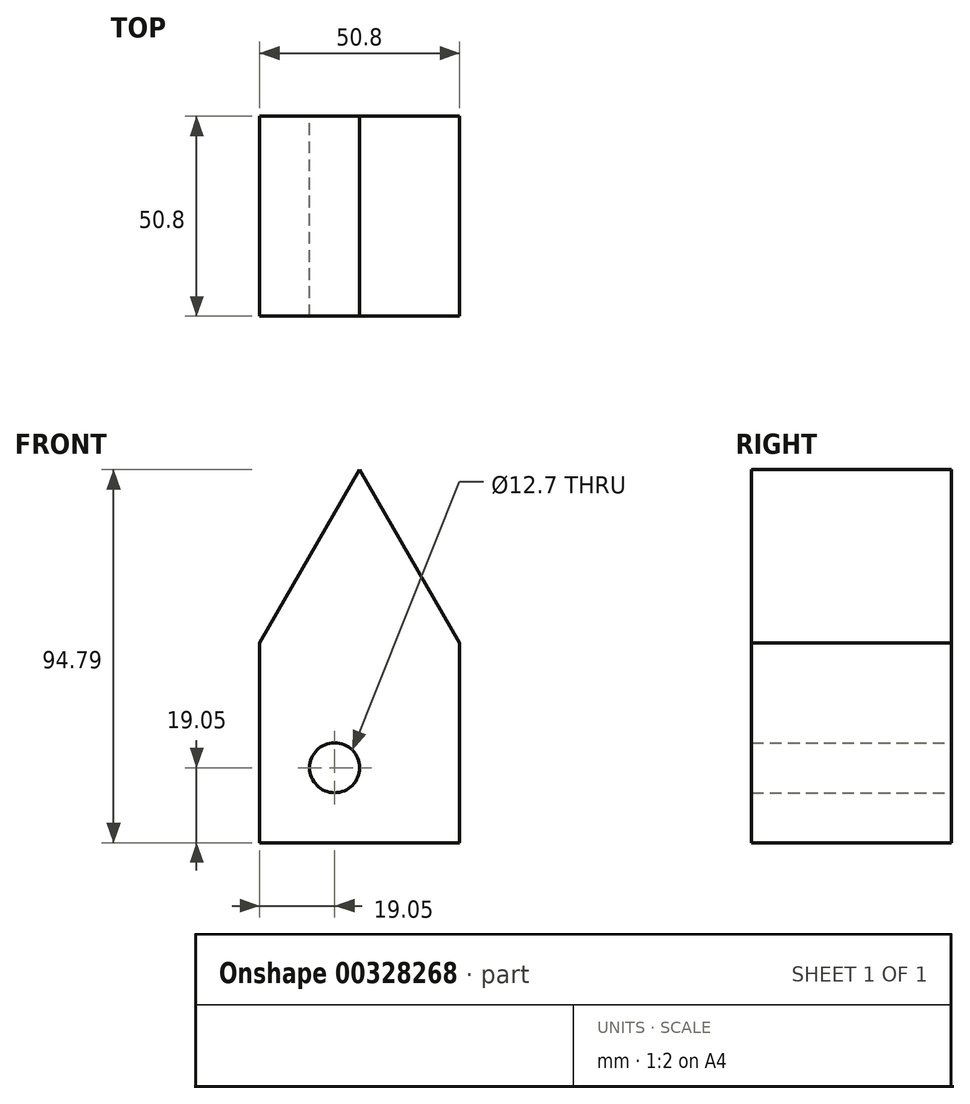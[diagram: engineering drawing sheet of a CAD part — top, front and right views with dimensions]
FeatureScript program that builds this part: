
annotation { "Feature Type Name" : "Feature", "Feature Type Description" : "" }
export const myFeature = defineFeature(function(context is Context, id is Id, definition is map)
    precondition{}
    {
        {
            var Q0;
            Q0=qCreatedBy(makeId("Front.planeOp"),FACE);
            var sketch = newSketch(context, id + "F0", { "sketchPlane" : qUnion([Q0])});
            skLineSegment(sketch, "E0.bottom", {"start": v(0, 0) * mm, "end": v(-50.8, 0) * mm});
            skLineSegment(sketch, "E0.left", {"start": v(0, 0) * mm, "end": v(0, 50.8) * mm});
            skLineSegment(sketch, "E0.right", {"start": v(-50.8, 0) * mm, "end": v(-50.8, 50.8) * mm});
            skLineSegment(sketch, "E1", {"start": v(-50.8, 50.8) * mm, "end": v(-25.4, 94.8) * mm});
            skLineSegment(sketch, "E2", {"start": v(0, 50.8) * mm, "end": v(-25.4, 94.8) * mm});
            skLineSegment(sketch, "E3", {"start": v(-31.75, 12.7) * mm, "end": v(-31.75, 19.05) * mm});
            skLineSegment(sketch, "E4", {"start": v(-38.1, 19.05) * mm, "end": v(-31.75, 19.05) * mm});
            skCircle(sketch, "E5", {"center": v(-31.75, 19.05) * mm, "radius": 6.35 * mm});
            skPoint(sketch, "E6.orphan", {"position": v(-50.8, 19.05) * mm});
            skSolve(sketch);
        }
        {
            var Q0;
            Q0=makeQuery(id+"F0.imprint","IMPRINT",FACE,{"disambiguationData":[TD([[makeQuery(id+"F0.imprint","IMPRINT",EDGE,{"derivedFrom":sQuery(id+"F0.wireOp",EDGE,"E0.bottom")}),-1.0]])]});
            extrude(context, id + "F1", {"entities" : qUnion([Q0]), "depth" : 50.8 * mm});
        }
    });
